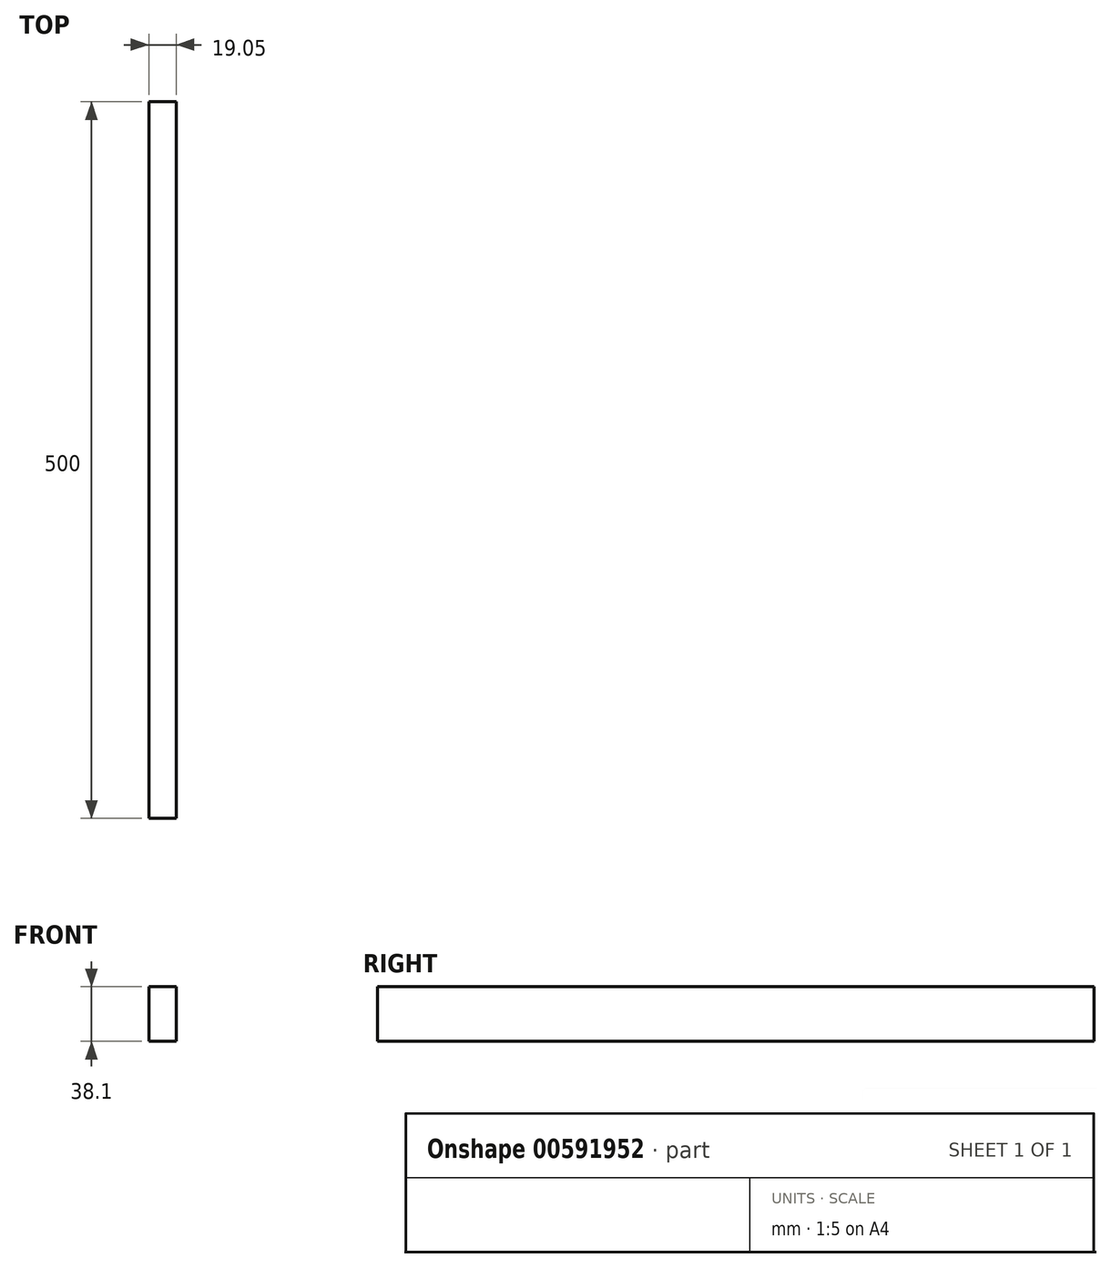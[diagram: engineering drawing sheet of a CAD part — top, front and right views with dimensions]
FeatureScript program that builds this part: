
annotation { "Feature Type Name" : "Feature", "Feature Type Description" : "" }
export const myFeature = defineFeature(function(context is Context, id is Id, definition is map)
    precondition{}
    {
        {
            var Q0;
            Q0=qCreatedBy(makeId("Front.planeOp"),FACE);
            var sketch = newSketch(context, id + "F0", { "sketchPlane" : qUnion([Q0])});
            skLineSegment(sketch, "E0.bottom", {"start": v(0, 0) * mm, "end": v(19.05, 0) * mm});
            skLineSegment(sketch, "E0.top", {"start": v(0, 38.1) * mm, "end": v(19.05, 38.1) * mm});
            skLineSegment(sketch, "E0.left", {"start": v(0, 0) * mm, "end": v(0, 38.1) * mm});
            skLineSegment(sketch, "E0.right", {"start": v(19.05, 0) * mm, "end": v(19.05, 38.1) * mm});
            skSolve(sketch);
        }
        {
            var Q0;
            Q0 = qSketchRegion(id + "F0", true);
            extrude(context, id + "F1", {"entities" : qUnion([Q0]), "depth" : 500 * mm, "offsetDistance" : 25.4 * mm});
        }
    });
